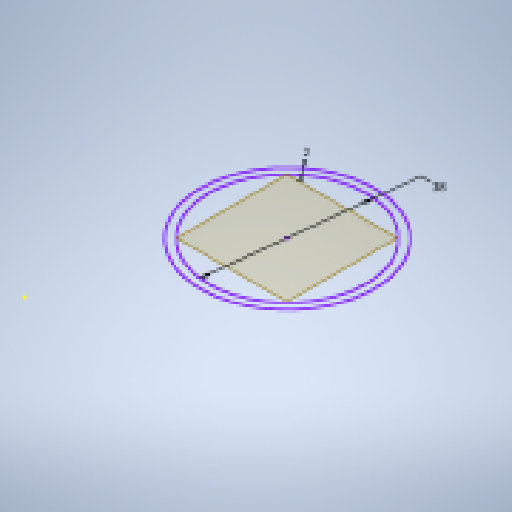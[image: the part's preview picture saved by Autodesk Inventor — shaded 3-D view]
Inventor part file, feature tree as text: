
AUTODESK INVENTOR PART (.ipt)
format: ipt  version: 2023.1 (Build 271208000, 208)  size: 130,048 bytes
history: native  units: in
note: dims shown in document units (in); Inventor stores cm internally (conversion verified against a paired STEP export)
features: other x3, plane x1, sketch x1
ambient origin geometry x8: Origin, YZ Plane, XZ Plane, XY Plane, X Axis, Y Axis, Z Axis, Center Point
feature tree (5):
  plane  "Work Plane1"
  sketch  "Sketch1"  dims[d0=1.4961in d1=0.0787in d2=0.0197in d3=0.0344in d4=0.0197in d5=0.0344in]
  other  "<userpath>\Documents\WaterPump\Assembly1.iam"
  other  "Assembly1.iam"
  other  "Motor:1"
